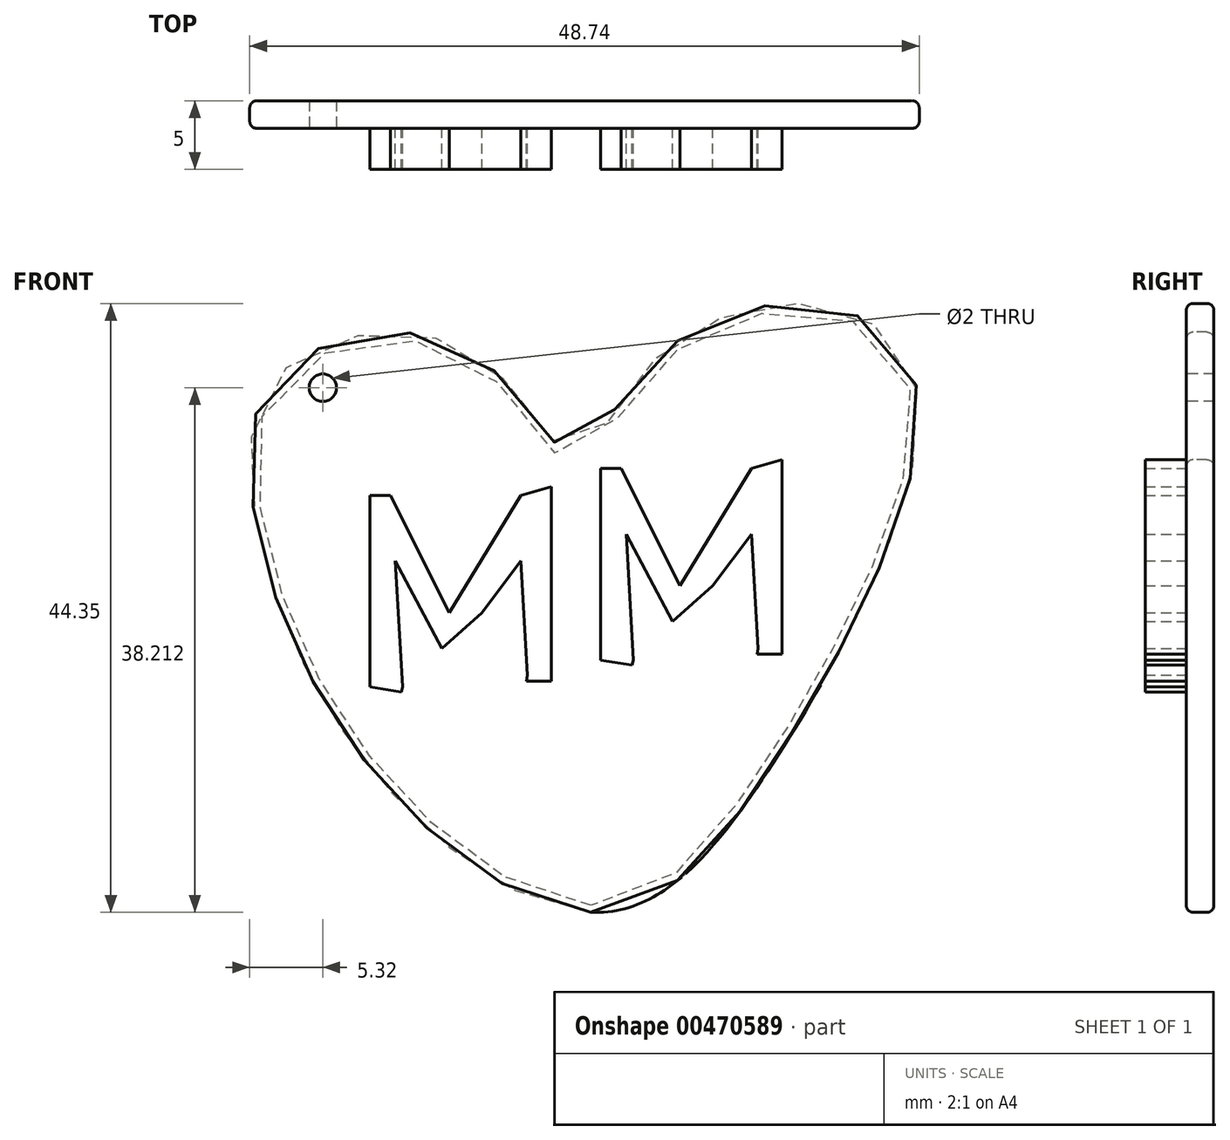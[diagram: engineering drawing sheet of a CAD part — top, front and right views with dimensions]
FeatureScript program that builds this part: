
annotation { "Feature Type Name" : "Feature", "Feature Type Description" : "" }
export const myFeature = defineFeature(function(context is Context, id is Id, definition is map)
    precondition{}
    {
        {
            var Q0;
            Q0=qCreatedBy(makeId("Front.planeOp"),FACE);
            var sketch = newSketch(context, id + "F0", { "sketchPlane" : qUnion([Q0])});
            skLineSegment(sketch, "E0", {"start": v(-16.07, 25.54) * mm, "end": v(-16.07, 11.6) * mm});
            skLineSegment(sketch, "E1", {"start": v(-16.07, 25.54) * mm, "end": v(-14.59, 25.54) * mm});
            skLineSegment(sketch, "E2", {"start": v(-14.59, 25.54) * mm, "end": v(-10.3, 17) * mm});
            skLineSegment(sketch, "E3", {"start": v(-10.3, 17) * mm, "end": v(-5.1, 25.54) * mm});
            skLineSegment(sketch, "E4", {"start": v(-5.1, 25.54) * mm, "end": v(-2.87, 26.17) * mm});
            skLineSegment(sketch, "E5", {"start": v(-2.87, 12.02) * mm, "end": v(-4.67, 12.02) * mm});
            skLineSegment(sketch, "E6", {"start": v(-4.62, 12.44) * mm, "end": v(-5.1, 20.77) * mm});
            skLineSegment(sketch, "E7", {"start": v(-5.1, 20.77) * mm, "end": v(-7.9, 17) * mm});
            skLineSegment(sketch, "E8", {"start": v(-10.82, 14.4) * mm, "end": v(-14.22, 20.77) * mm});
            skLineSegment(sketch, "E9", {"start": v(-14.22, 20.77) * mm, "end": v(-13.7, 11.6) * mm});
            skLineSegment(sketch, "E10", {"start": v(-13.8, 11.22) * mm, "end": v(-16.07, 11.6) * mm});
            skLineSegment(sketch, "E11", {"start": v(0.73, 27.49) * mm, "end": v(0.73, 13.55) * mm});
            skLineSegment(sketch, "E12", {"start": v(0.73, 27.49) * mm, "end": v(2.21, 27.49) * mm});
            skLineSegment(sketch, "E13", {"start": v(2.21, 27.49) * mm, "end": v(6.5, 18.95) * mm});
            skLineSegment(sketch, "E14", {"start": v(6.5, 18.95) * mm, "end": v(11.7, 27.49) * mm});
            skLineSegment(sketch, "E15", {"start": v(11.7, 27.49) * mm, "end": v(13.93, 28.12) * mm});
            skLineSegment(sketch, "E16", {"start": v(13.93, 13.97) * mm, "end": v(12.12, 13.97) * mm});
            skLineSegment(sketch, "E17", {"start": v(12.18, 14.4) * mm, "end": v(11.7, 22.72) * mm});
            skLineSegment(sketch, "E18", {"start": v(11.7, 22.72) * mm, "end": v(8.9, 18.95) * mm});
            skLineSegment(sketch, "E19", {"start": v(5.97, 16.36) * mm, "end": v(2.58, 22.72) * mm});
            skLineSegment(sketch, "E20", {"start": v(2.58, 22.72) * mm, "end": v(3.1, 13.55) * mm});
            skLineSegment(sketch, "E21", {"start": v(3, 13.17) * mm, "end": v(0.73, 13.55) * mm});
            skLineSegment(sketch, "E22", {"start": v(-2.87, 12.02) * mm, "end": v(-2.87, 26.17) * mm});
            skLineSegment(sketch, "E23", {"start": v(-4.67, 12.02) * mm, "end": v(-4.62, 12.44) * mm});
            skLineSegment(sketch, "E24", {"start": v(-13.8, 11.22) * mm, "end": v(-13.7, 11.6) * mm});
            skLineSegment(sketch, "E25", {"start": v(3, 13.17) * mm, "end": v(3.1, 13.55) * mm});
            skLineSegment(sketch, "E26", {"start": v(12.12, 13.97) * mm, "end": v(12.18, 14.4) * mm});
            skLineSegment(sketch, "E27", {"start": v(13.93, 13.97) * mm, "end": v(13.93, 28.12) * mm});
            skLineSegment(sketch, "E28", {"start": v(8.9, 18.95) * mm, "end": v(5.97, 16.36) * mm});
            skLineSegment(sketch, "E29", {"start": v(-7.9, 17) * mm, "end": v(-10.82, 14.4) * mm});
            skSolve(sketch);
        }
        {
            var Q0;
            Q0 = qSketchRegion(id + "F0", true);
            extrude(context, id + "F1", {"entities" : qUnion([Q0]), "depth" : 3 * mm});
        }
        {
            var Q0;
            Q0=qCreatedBy(makeId("Front.planeOp"),FACE);
            var sketch = newSketch(context, id + "F2", { "sketchPlane" : qUnion([Q0])});
            skFitSpline(sketch, "E30", {"points": [v(0, -4.82) * mm, v(-18.64, 9.27) * mm, v(-24.66, 30.26) * mm, v(-21.08, 35.59) * mm, v(-13.43, 37.39) * mm, v(-5.77, 33.4) * mm, v(-0.94, 28.14) * mm, v(2.71, 33.32) * mm, v(14.1, 39.5) * mm, v(23.6, 34) * mm, v(12.78, 5.29) * mm, v(0, -4.82) * mm]});
            skSolve(sketch);
        }
        {
            var Q0;
            Q0 = qSketchRegion(id + "F2", true);
            extrude(context, id + "F3", {"entities" : qUnion([Q0]), "depth" : -2 * mm});
        }
        {
            var Q0;
            Q0=qCreatedBy(makeId("Front.planeOp"),FACE);
            var sketch = newSketch(context, id + "F4", { "sketchPlane" : qUnion([Q0])});
            skCircle(sketch, "E31", {"center": v(-19.5, 33.38) * mm, "radius": 1.5 * mm});
            skSolve(sketch);
        }
        {
            var Q0;
            Q0=sQuery(id+"F4.wireOp",VERTEX,"E31.center");
            var Q1;
            Q1=makeQuery(id+"F3.opExtrude","SWEPT_BODY",BODY,{"disambiguationData":[OSD([sQuery(id+"F2.wireOp",EDGE,"E30")])]});
            hole(context, id + "F5", {"style" : HoleStyle.SIMPLE, "endStyle" : HoleEndStyle.THROUGH, "holeDiameter" : 2 * mm, "isTappedThrough" : true, "tappedDepth" : 12 * mm, "tapClearance" : 3, "locations" : qUnion([Q0]), "scope" : qUnion([Q1])});
        }
        {
            var Q0;
            Q0=makeQuery(id+"F3.opExtrude","CAP_EDGE",EDGE,{"disambiguationData":[OSD([sQuery(id+"F2.wireOp",EDGE,"E30")])],"isStart":true});
            fillet(context, id + "F6", {"entities" : qUnion([Q0]), "radius" : 0.5 * mm, "tangentPropagation" : true, "allowEdgeOverflow" : false});
        }
        {
            var Q0;
            Q0=makeQuery(id+"F3.opExtrude","CAP_EDGE",EDGE,{"disambiguationData":[OSD([sQuery(id+"F2.wireOp",EDGE,"E30")])],"isStart":false});
            fillet(context, id + "F7", {"entities" : qUnion([Q0]), "radius" : 0.5 * mm, "tangentPropagation" : true, "allowEdgeOverflow" : false});
        }
    });
